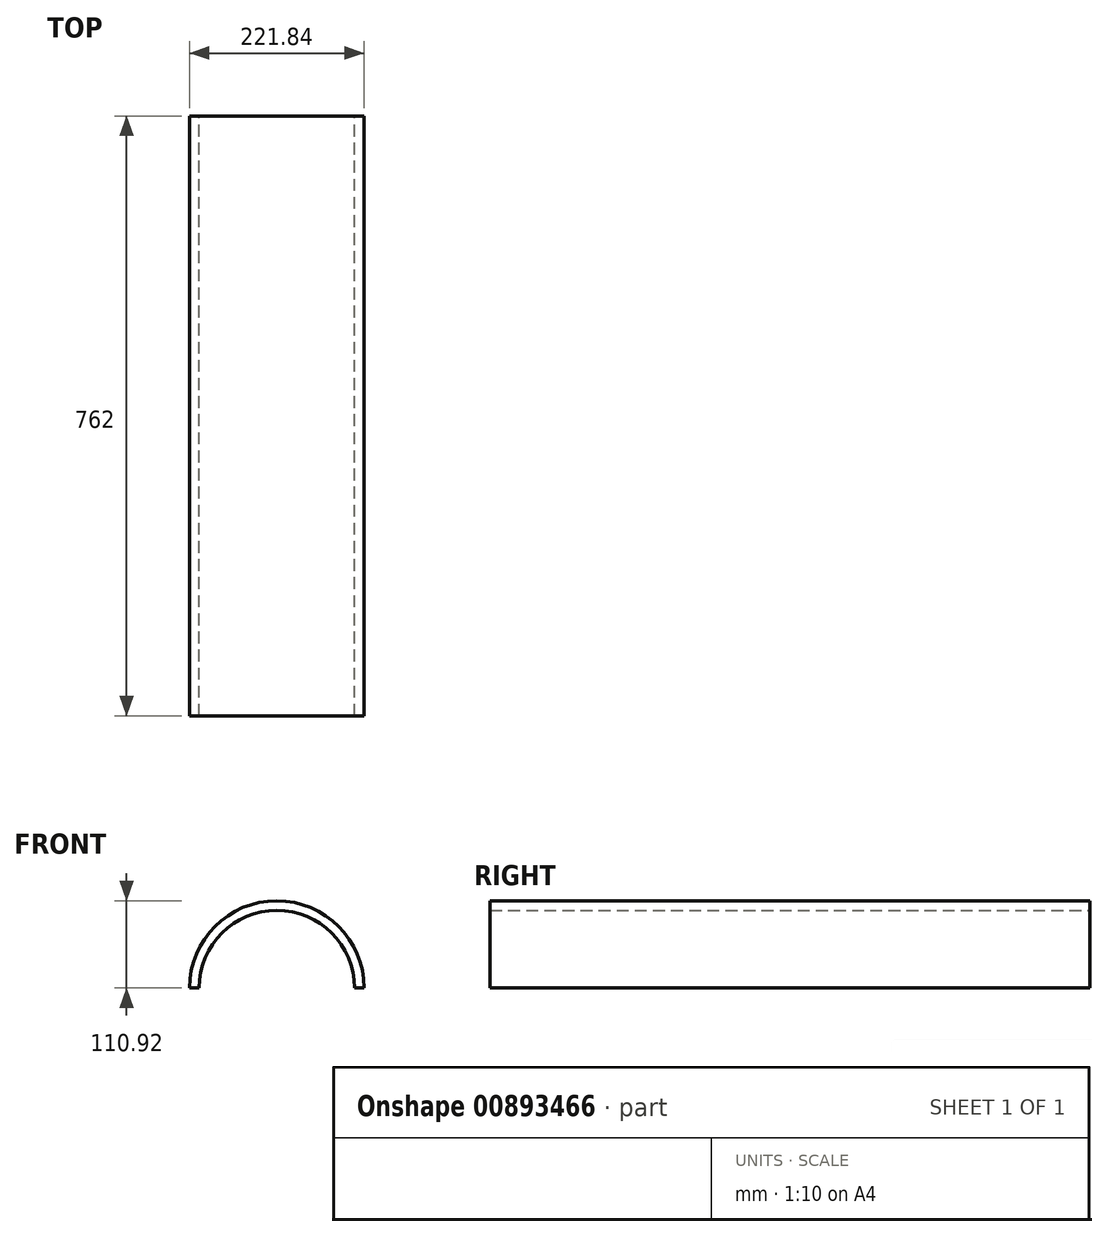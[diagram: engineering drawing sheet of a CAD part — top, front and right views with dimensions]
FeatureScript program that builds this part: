
annotation { "Feature Type Name" : "Feature", "Feature Type Description" : "" }
export const myFeature = defineFeature(function(context is Context, id is Id, definition is map)
    precondition{}
    {
        {
            var Q0;
            Q0=qCreatedBy(makeId("Front.planeOp"),FACE);
            var sketch = newSketch(context, id + "F0", { "sketchPlane" : qUnion([Q0])});
            skCircle(sketch, "E0", {"center": v(0, 0) * mm, "radius": 110.92 * mm});
            skCircle(sketch, "E1", {"center": v(0, 0) * mm, "radius": 98.67 * mm});
            skLineSegment(sketch, "E2", {"start": v(0, 0) * mm, "end": v(-110.92, 0) * mm});
            skLineSegment(sketch, "E3", {"start": v(0, 0) * mm, "end": v(110.92, 0) * mm});
            skSolve(sketch);
        }
        {
            var Q0;
            {var subQ0=sQuery(id+"F0.wireOp",EDGE,"E2");var subQ1=sQuery(id+"F0.wireOp",EDGE,"E0");var subQ2=makeQuery(id+"F0.imprint","INTERSECT",VERTEX,{"derivedFrom":[subQ1,subQ0]});Q0=makeQuery(id+"F0.imprint","IMPRINT",FACE,{"disambiguationData":[TD([[makeQuery(id+"F0.imprint","IMPRINT",EDGE,{"disambiguationData":[TD([[subQ2,1.0]])],"derivedFrom":subQ1}),1.0]])]});}
            extrude(context, id + "F1", {"entities" : qUnion([Q0]), "depth" : 762 * mm, "offsetDistance" : 25.4 * mm});
        }
    });
